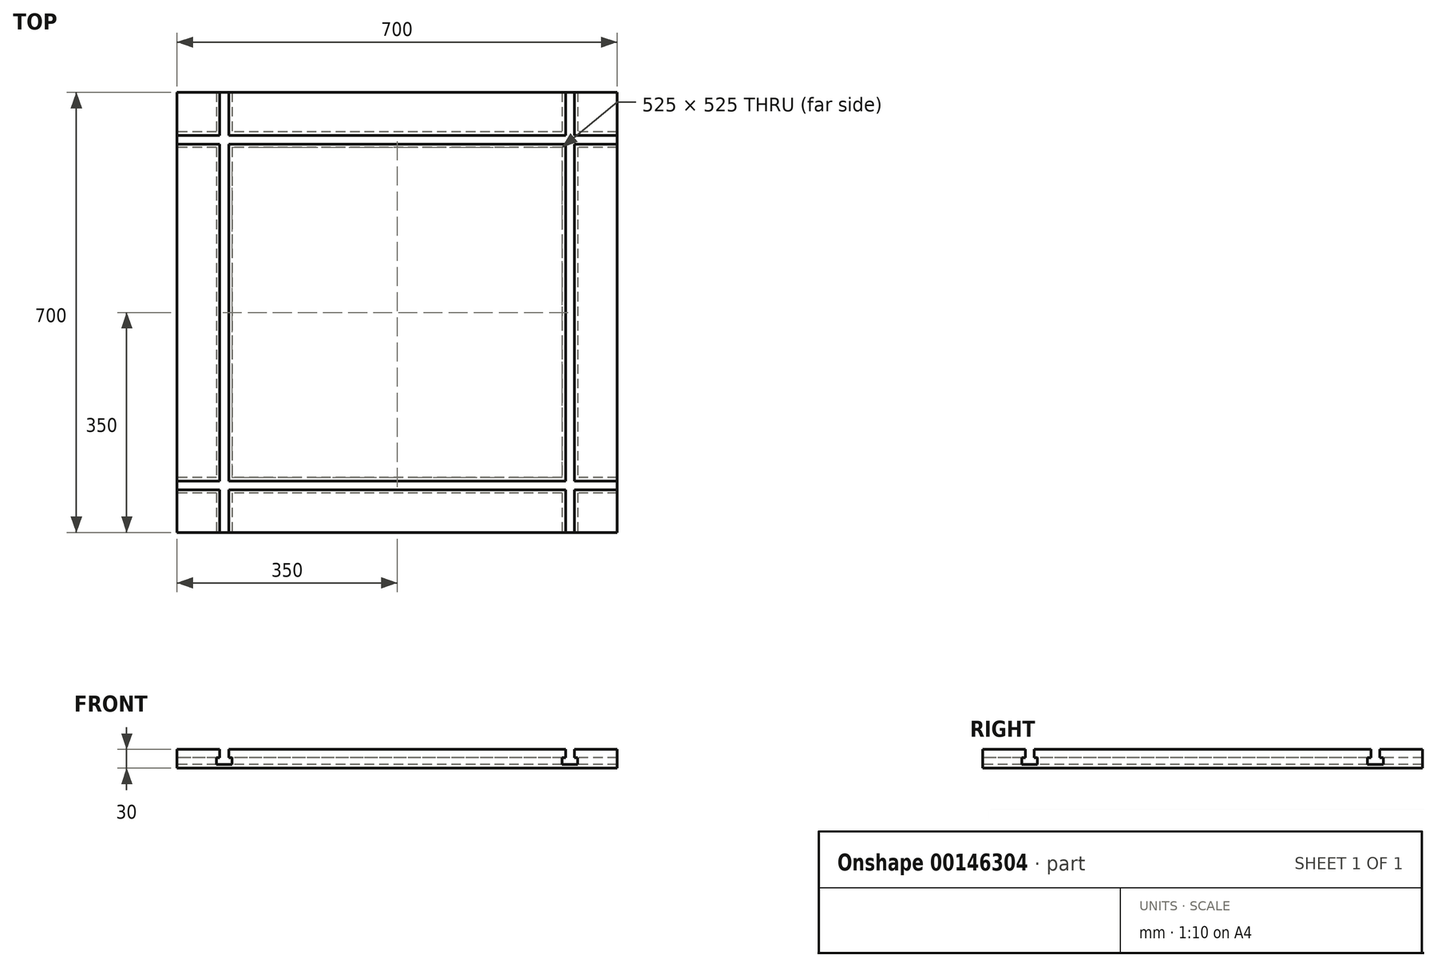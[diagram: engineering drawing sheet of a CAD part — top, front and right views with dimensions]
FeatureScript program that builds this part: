
annotation { "Feature Type Name" : "Feature", "Feature Type Description" : "" }
export const myFeature = defineFeature(function(context is Context, id is Id, definition is map)
    precondition{}
    {
        {
            var Q0;
            Q0=qCreatedBy(makeId("Front.planeOp"),FACE);
            var sketch = newSketch(context, id + "F0", { "sketchPlane" : qUnion([Q0])});
            skLineSegment(sketch, "E0.bottom", {"start": v(350, 15) * mm, "end": v(-350, 15) * mm});
            skLineSegment(sketch, "E0.top", {"start": v(350, -15) * mm, "end": v(-350, -15) * mm});
            skLineSegment(sketch, "E0.left", {"start": v(350, 15) * mm, "end": v(350, -15) * mm});
            skLineSegment(sketch, "E0.right", {"start": v(-350, 15) * mm, "end": v(-350, -15) * mm});
            skPoint(sketch, "E0.middle", {"position": v(0, 0) * mm});
            skLineSegment(sketch, "E1", {"start": v(-282, 15) * mm, "end": v(-282, 2) * mm});
            skLineSegment(sketch, "E2", {"start": v(-282, 2) * mm, "end": v(-287.5, 2) * mm});
            skLineSegment(sketch, "E3", {"start": v(-287.5, 2) * mm, "end": v(-287.5, -9) * mm});
            skLineSegment(sketch, "E4", {"start": v(-287.5, -9) * mm, "end": v(-262.5, -9) * mm});
            skLineSegment(sketch, "E5", {"start": v(-262.5, -9) * mm, "end": v(-262.5, 2) * mm});
            skLineSegment(sketch, "E6", {"start": v(-262.5, 2) * mm, "end": v(-268, 2) * mm});
            skLineSegment(sketch, "E7", {"start": v(-268, 2) * mm, "end": v(-268, 15) * mm});
            skLineSegment(sketch, "E8", {"start": v(-275, 12.58) * mm, "end": v(-275, 2.42) * mm, "construction": true});
            skLineSegment(sketch, "E9.MirrorCS", {"start": v(282, 2) * mm, "end": v(287.5, 2) * mm});
            skLineSegment(sketch, "E10.MirrorCS", {"start": v(287.5, 2) * mm, "end": v(287.5, -9) * mm});
            skLineSegment(sketch, "E11.MirrorCS", {"start": v(287.5, -9) * mm, "end": v(262.5, -9) * mm});
            skLineSegment(sketch, "E12.MirrorCS", {"start": v(262.5, -9) * mm, "end": v(262.5, 2) * mm});
            skLineSegment(sketch, "E13.MirrorCS", {"start": v(262.5, 2) * mm, "end": v(268, 2) * mm});
            skLineSegment(sketch, "E14.MirrorCS", {"start": v(282, 15) * mm, "end": v(282, 2) * mm});
            skLineSegment(sketch, "E15.MirrorCS", {"start": v(268, 2) * mm, "end": v(268, 15) * mm});
            skLineSegment(sketch, "E16", {"start": v(275, 12.82) * mm, "end": v(275, 3.84) * mm, "construction": true});
            skSolve(sketch);
        }
        {
            var Q0;
            Q0=makeQuery(id+"F0.imprint","IMPRINT",FACE,{"disambiguationData":[TD([[makeQuery(id+"F0.imprint","IMPRINT",EDGE,{"derivedFrom":sQuery(id+"F0.wireOp",EDGE,"E0.top")}),-1.0]])]});
            extrude(context, id + "F1", {"entities" : qUnion([Q0]), "oppositeDirection" : true, "depth" : 700 * mm});
        }
        {
            var Q0;
            Q0=makeQuery(id+"F1.opExtrude","SWEPT_FACE",FACE,{"disambiguationData":[OSD([sQuery(id+"F0.wireOp",EDGE,"E0.right")])]});
            var sketch = newSketch(context, id + "F2", { "sketchPlane" : qUnion([Q0])});
            skLineSegment(sketch, "E17.bottom", {"start": v(0, 15) * mm, "end": v(-700, 15) * mm});
            skLineSegment(sketch, "E17.top", {"start": v(0, -15) * mm, "end": v(-700, -15) * mm});
            skLineSegment(sketch, "E17.left", {"start": v(0, 15) * mm, "end": v(0, -15) * mm});
            skLineSegment(sketch, "E17.right", {"start": v(-700, 15) * mm, "end": v(-700, -15) * mm});
            skPoint(sketch, "E17.middle", {"position": v(-350, 0) * mm});
            skLineSegment(sketch, "E18", {"start": v(-632, 15) * mm, "end": v(-632, 2) * mm});
            skLineSegment(sketch, "E19", {"start": v(-632, 2) * mm, "end": v(-637.5, 2) * mm});
            skLineSegment(sketch, "E20", {"start": v(-637.5, 2) * mm, "end": v(-637.5, -9) * mm});
            skLineSegment(sketch, "E21", {"start": v(-637.5, -9) * mm, "end": v(-612.5, -9) * mm});
            skLineSegment(sketch, "E22", {"start": v(-612.5, -9) * mm, "end": v(-612.5, 2) * mm});
            skLineSegment(sketch, "E23", {"start": v(-612.5, 2) * mm, "end": v(-618, 2) * mm});
            skLineSegment(sketch, "E24", {"start": v(-618, 2) * mm, "end": v(-618, 15) * mm});
            skLineSegment(sketch, "E25", {"start": v(-625, 12.58) * mm, "end": v(-625, 2.42) * mm, "construction": true});
            skLineSegment(sketch, "E26.MirrorCS", {"start": v(-68, 2) * mm, "end": v(-62.5, 2) * mm});
            skLineSegment(sketch, "E27.MirrorCS", {"start": v(-62.5, 2) * mm, "end": v(-62.5, -9) * mm});
            skLineSegment(sketch, "E28.MirrorCS", {"start": v(-62.5, -9) * mm, "end": v(-87.5, -9) * mm});
            skLineSegment(sketch, "E29.MirrorCS", {"start": v(-87.5, -9) * mm, "end": v(-87.5, 2) * mm});
            skLineSegment(sketch, "E30.MirrorCS", {"start": v(-87.5, 2) * mm, "end": v(-82, 2) * mm});
            skLineSegment(sketch, "E31.MirrorCS", {"start": v(-68, 15) * mm, "end": v(-68, 2) * mm});
            skLineSegment(sketch, "E32.MirrorCS", {"start": v(-82, 2) * mm, "end": v(-82, 15) * mm});
            skLineSegment(sketch, "E33", {"start": v(-75, 12.82) * mm, "end": v(-75, 3.84) * mm, "construction": true});
            skSolve(sketch);
        }
        {
            var Q0;
            {var subQ0=sQuery(id+"F2.wireOp",EDGE,"E18");Q0=makeQuery(id+"F2.imprint","IMPRINT",FACE,{"disambiguationData":[TD([[makeQuery(id+"F2.imprint","IMPRINT",EDGE,{"derivedFrom":subQ0}),1.0]])]});}
            var Q1;
            Q1=makeQuery(id+"F2.imprint","IMPRINT",FACE,{"disambiguationData":[TD([[makeQuery(id+"F2.imprint","IMPRINT",EDGE,{"derivedFrom":sQuery(id+"F2.wireOp",EDGE,"E26.MirrorCS")}),-1.0]])]});
            extrude(context, id + "F3", {"entities" : qUnion([Q0, Q1]), "operationType" : NewBodyOperationType.REMOVE, "oppositeDirection" : true, "depth" : 700 * mm});
        }
    });
